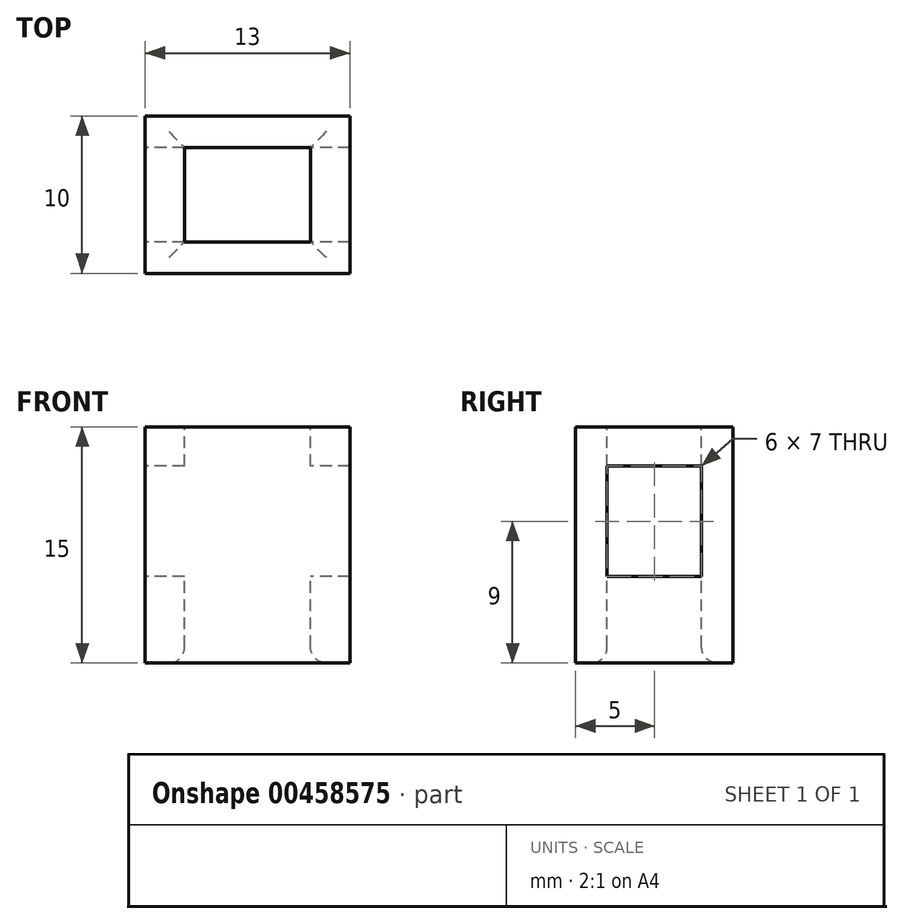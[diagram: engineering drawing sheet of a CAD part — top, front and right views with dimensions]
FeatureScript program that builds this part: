
annotation { "Feature Type Name" : "Feature", "Feature Type Description" : "" }
export const myFeature = defineFeature(function(context is Context, id is Id, definition is map)
    precondition{}
    {
        {
            var Q0;
            Q0=qCreatedBy(makeId("Top.planeOp"),FACE);
            var sketch = newSketch(context, id + "F0", { "sketchPlane" : qUnion([Q0])});
            skLineSegment(sketch, "E0.bottom", {"start": v(-6.5, 5) * mm, "end": v(6.5, 5) * mm});
            skLineSegment(sketch, "E0.top", {"start": v(-6.5, -5) * mm, "end": v(6.5, -5) * mm});
            skLineSegment(sketch, "E0.left", {"start": v(-6.5, 5) * mm, "end": v(-6.5, -5) * mm});
            skLineSegment(sketch, "E0.right", {"start": v(6.5, 5) * mm, "end": v(6.5, -5) * mm});
            skPoint(sketch, "E0.middle", {"position": v(0, 0) * mm});
            skSolve(sketch);
        }
        {
            var Q0;
            Q0 = qSketchRegion(id + "F0", true);
            extrude(context, id + "F1", {"entities" : qUnion([Q0]), "depth" : 15 * mm, "offsetDistance" : 25 * mm});
        }
        {
            var Q0;
            Q0=makeQuery(id+"F1.opExtrude","CAP_FACE",FACE,{"disambiguationData":[OSD([sQuery(id+"F0.wireOp",EDGE,"E0.bottom"),sQuery(id+"F0.wireOp",EDGE,"E0.top"),sQuery(id+"F0.wireOp",EDGE,"E0.left"),sQuery(id+"F0.wireOp",EDGE,"E0.right")])],"isStart":false});
            var sketch = newSketch(context, id + "F2", { "sketchPlane" : qUnion([Q0])});
            skLineSegment(sketch, "E1.bottom", {"start": v(-4, 3) * mm, "end": v(4, 3) * mm});
            skLineSegment(sketch, "E1.top", {"start": v(-4, -3) * mm, "end": v(4, -3) * mm});
            skLineSegment(sketch, "E1.left", {"start": v(-4, 3) * mm, "end": v(-4, -3) * mm});
            skLineSegment(sketch, "E1.right", {"start": v(4, 3) * mm, "end": v(4, -3) * mm});
            skPoint(sketch, "E1.middle", {"position": v(0, 0) * mm});
            skSolve(sketch);
        }
        {
            var Q0;
            Q0 = qSketchRegion(id + "F2", true);
            extrude(context, id + "F3", {"entities" : qUnion([Q0]), "operationType" : NewBodyOperationType.REMOVE, "oppositeDirection" : true, "depth" : 25 * mm, "offsetDistance" : 25 * mm});
        }
        {
            var Q0;
            Q0=makeQuery(id+"F1.opExtrude","SWEPT_FACE",FACE,{"disambiguationData":[OSD([sQuery(id+"F0.wireOp",EDGE,"E0.left")])]});
            var sketch = newSketch(context, id + "F4", { "sketchPlane" : qUnion([Q0])});
            skLineSegment(sketch, "E2.bottom", {"start": v(3, 5.5) * mm, "end": v(-3, 5.5) * mm});
            skLineSegment(sketch, "E2.top", {"start": v(3, 12.5) * mm, "end": v(-3, 12.5) * mm});
            skLineSegment(sketch, "E2.left", {"start": v(3, 5.5) * mm, "end": v(3, 12.5) * mm});
            skLineSegment(sketch, "E2.right", {"start": v(-3, 5.5) * mm, "end": v(-3, 12.5) * mm});
            skSolve(sketch);
        }
        {
            var Q0;
            Q0 = qSketchRegion(id + "F4", true);
            extrude(context, id + "F5", {"entities" : qUnion([Q0]), "operationType" : NewBodyOperationType.REMOVE, "oppositeDirection" : true, "depth" : 13 * mm, "offsetDistance" : 25 * mm});
        }
        {
            var Q0;
            Q0=makeQuery(id+"F3.boolean.opBoolean","INTERSECT",EDGE,{"derivedFrom":[makeQuery(id+"F1.opExtrude","CAP_FACE",FACE,{"disambiguationData":[OSD([sQuery(id+"F0.wireOp",EDGE,"E0.bottom"),sQuery(id+"F0.wireOp",EDGE,"E0.top"),sQuery(id+"F0.wireOp",EDGE,"E0.left"),sQuery(id+"F0.wireOp",EDGE,"E0.right")])],"isStart":true}),makeQuery(id+"F3.opExtrude","SWEPT_FACE",FACE,{"disambiguationData":[OSD([sQuery(id+"F2.wireOp",EDGE,"E1.right")])]})]});
            var Q1;
            Q1=makeQuery(id+"F3.boolean.opBoolean","INTERSECT",EDGE,{"derivedFrom":[makeQuery(id+"F1.opExtrude","CAP_FACE",FACE,{"disambiguationData":[OSD([sQuery(id+"F0.wireOp",EDGE,"E0.bottom"),sQuery(id+"F0.wireOp",EDGE,"E0.top"),sQuery(id+"F0.wireOp",EDGE,"E0.left"),sQuery(id+"F0.wireOp",EDGE,"E0.right")])],"isStart":true}),makeQuery(id+"F3.opExtrude","SWEPT_FACE",FACE,{"disambiguationData":[OSD([sQuery(id+"F2.wireOp",EDGE,"E1.bottom")])]})]});
            var Q2;
            Q2=makeQuery(id+"F3.boolean.opBoolean","INTERSECT",EDGE,{"derivedFrom":[makeQuery(id+"F1.opExtrude","CAP_FACE",FACE,{"disambiguationData":[OSD([sQuery(id+"F0.wireOp",EDGE,"E0.bottom"),sQuery(id+"F0.wireOp",EDGE,"E0.top"),sQuery(id+"F0.wireOp",EDGE,"E0.left"),sQuery(id+"F0.wireOp",EDGE,"E0.right")])],"isStart":true}),makeQuery(id+"F3.opExtrude","SWEPT_FACE",FACE,{"disambiguationData":[OSD([sQuery(id+"F2.wireOp",EDGE,"E1.left")])]})]});
            var Q3;
            Q3=makeQuery(id+"F3.boolean.opBoolean","INTERSECT",EDGE,{"derivedFrom":[makeQuery(id+"F1.opExtrude","CAP_FACE",FACE,{"disambiguationData":[OSD([sQuery(id+"F0.wireOp",EDGE,"E0.bottom"),sQuery(id+"F0.wireOp",EDGE,"E0.top"),sQuery(id+"F0.wireOp",EDGE,"E0.left"),sQuery(id+"F0.wireOp",EDGE,"E0.right")])],"isStart":true}),makeQuery(id+"F3.opExtrude","SWEPT_FACE",FACE,{"disambiguationData":[OSD([sQuery(id+"F2.wireOp",EDGE,"E1.top")])]})]});
            fillet(context, id + "F6", {"entities" : qUnion([Q0, Q1, Q2, Q3]), "radius" : 1 * mm, "tangentPropagation" : true, "allowEdgeOverflow" : false});
        }
    });
